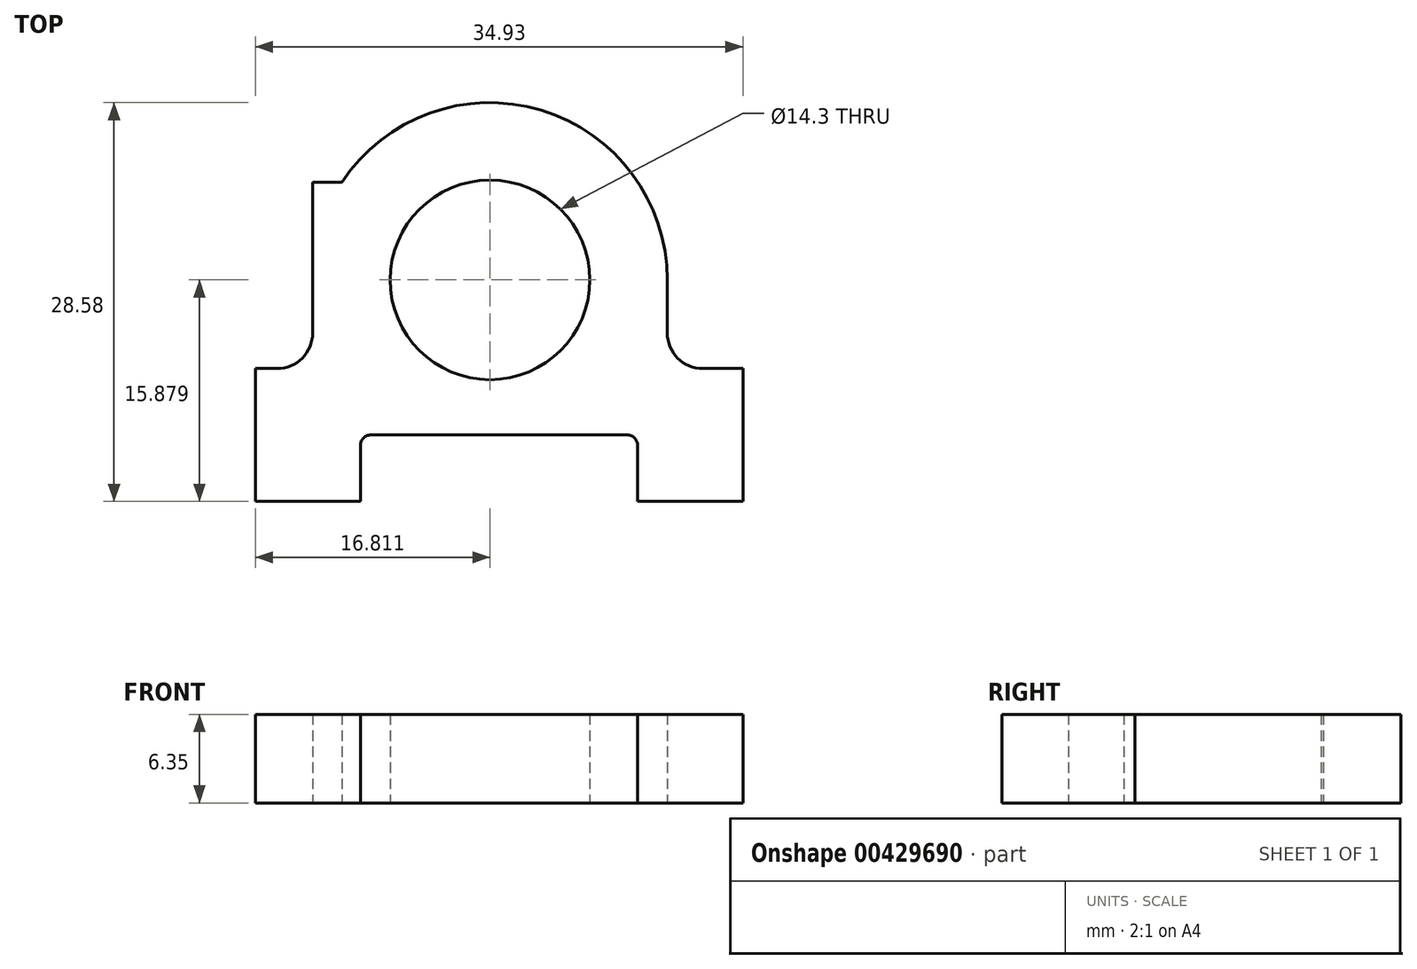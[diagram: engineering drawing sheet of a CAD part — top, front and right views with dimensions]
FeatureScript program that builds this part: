
annotation { "Feature Type Name" : "Feature", "Feature Type Description" : "" }
export const myFeature = defineFeature(function(context is Context, id is Id, definition is map)
    precondition{}
    {
        {
            var Q0;
            Q0=qCreatedBy(makeId("Top.planeOp"),FACE);
            var sketch = newSketch(context, id + "F0", { "sketchPlane" : qUnion([Q0])});
            skLineSegment(sketch, "E0.bottom", {"start": v(-111.37, 43.65) * mm, "end": v(-109.8, 43.65) * mm});
            skLineSegment(sketch, "E0.top", {"start": v(-111.37, 34.12) * mm, "end": v(-103.84, 34.12) * mm});
            skLineSegment(sketch, "E0.left", {"start": v(-111.37, 43.65) * mm, "end": v(-111.37, 34.12) * mm});
            skLineSegment(sketch, "E0.right", {"start": v(-76.44, 43.65) * mm, "end": v(-76.44, 34.12) * mm});
            skPoint(sketch, "E1", {"position": v(-93.9, 43.65) * mm});
            skLineSegment(sketch, "E2.left", {"start": v(-107.26, 46.19) * mm, "end": v(-107.26, 50) * mm});
            skLineSegment(sketch, "E2.right", {"start": v(-81.86, 46.19) * mm, "end": v(-81.86, 50) * mm});
            skArc(sketch, "E3", {"start": v(-81.86, 50) * mm, "mid": v(-90.9, 62.16) * mm, "end": v(-105.16, 57) * mm});
            skCircle(sketch, "E4", {"center": v(-94.56, 50) * mm, "radius": 7.15 * mm});
            skLineSegment(sketch, "E5.trimOffspring", {"start": v(-79.32, 43.65) * mm, "end": v(-76.44, 43.65) * mm});
            skLineSegment(sketch, "E6.top", {"start": v(-107.26, 57) * mm, "end": v(-105.16, 57) * mm});
            skLineSegment(sketch, "E6.left", {"start": v(-107.26, 50) * mm, "end": v(-107.26, 57) * mm});
            skPoint(sketch, "E7.oppositeSnap0", {"position": v(-76.44, 38.89) * mm});
            skLineSegment(sketch, "E7.top", {"start": v(-103.08, 38.89) * mm, "end": v(-84.74, 38.89) * mm});
            skLineSegment(sketch, "E7.left", {"start": v(-103.84, 34.12) * mm, "end": v(-103.84, 38.12) * mm});
            skLineSegment(sketch, "E7.right", {"start": v(-83.98, 34.12) * mm, "end": v(-83.98, 38.12) * mm});
            skLineSegment(sketch, "E8.trimOffspring", {"start": v(-83.98, 34.12) * mm, "end": v(-76.44, 34.12) * mm});
            skPoint(sketch, "E9.visualSharp", {"position": v(-103.84, 38.89) * mm});
            skArc(sketch, "E9.filletArc", {"start": v(-103.08, 38.89) * mm, "mid": v(-103.62, 38.66) * mm, "end": v(-103.84, 38.12) * mm});
            skPoint(sketch, "E10.visualSharp", {"position": v(-83.98, 38.89) * mm});
            skArc(sketch, "E10.filletArc", {"start": v(-83.98, 38.12) * mm, "mid": v(-84.2, 38.66) * mm, "end": v(-84.74, 38.89) * mm});
            skPoint(sketch, "E11.visualSharp", {"position": v(-107.26, 43.65) * mm});
            skArc(sketch, "E11.filletArc", {"start": v(-109.8, 43.65) * mm, "mid": v(-108, 44.4) * mm, "end": v(-107.26, 46.19) * mm});
            skPoint(sketch, "E12.visualSharp", {"position": v(-81.86, 43.65) * mm});
            skArc(sketch, "E12.filletArc", {"start": v(-81.86, 46.19) * mm, "mid": v(-81.12, 44.4) * mm, "end": v(-79.32, 43.65) * mm});
            skSolve(sketch);
        }
        {
            var Q0;
            Q0=makeQuery(id+"F0.imprint","IMPRINT",FACE,{"disambiguationData":[TD([[makeQuery(id+"F0.imprint","IMPRINT",EDGE,{"derivedFrom":sQuery(id+"F0.wireOp",EDGE,"E0.bottom")}),-1.0]])]});
            extrude(context, id + "F1", {"entities" : qUnion([Q0]), "depth" : 6.35 * mm});
        }
    });
